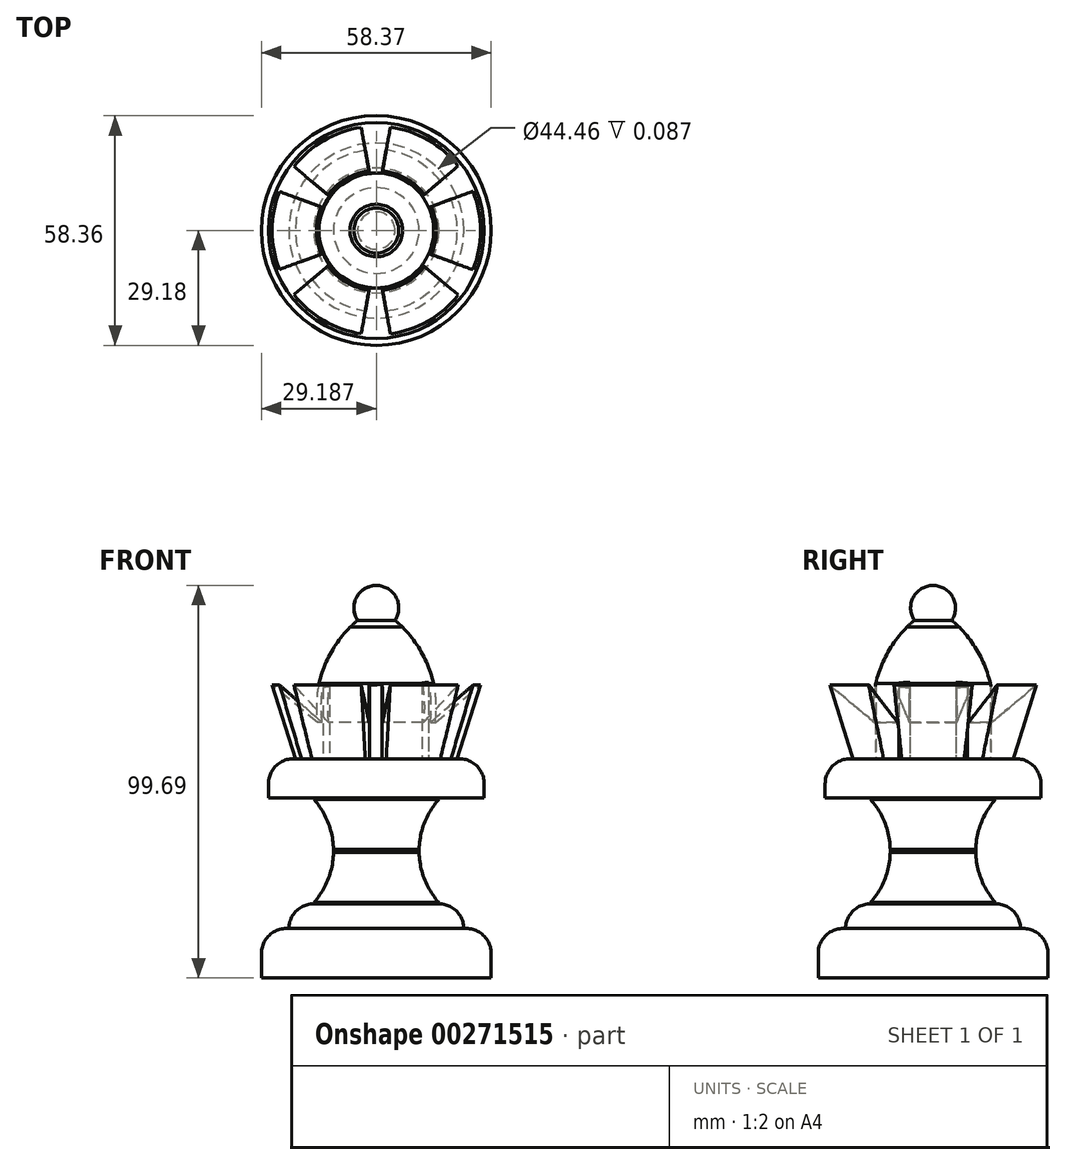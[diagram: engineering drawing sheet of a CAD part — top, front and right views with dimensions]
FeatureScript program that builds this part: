
annotation { "Feature Type Name" : "Feature", "Feature Type Description" : "" }
export const myFeature = defineFeature(function(context is Context, id is Id, definition is map)
    precondition{}
    {
        {
            var Q0;
            Q0=qCreatedBy(makeId("Front.planeOp"),FACE);
            var sketch = newSketch(context, id + "F0", { "sketchPlane" : qUnion([Q0])});
            skLineSegment(sketch, "E0.bottom", {"start": v(0.14, 0) * mm, "end": v(-29.05, 0) * mm});
            skLineSegment(sketch, "E0.top", {"start": v(-22.1, 12.55) * mm, "end": v(-22.7, 12.55) * mm});
            skLineSegment(sketch, "E0.right", {"start": v(-29.05, 0) * mm, "end": v(-29.05, 6.2) * mm});
            skLineSegment(sketch, "E1.bottom", {"start": v(-0.27, 12.55) * mm, "end": v(0, 12.55) * mm});
            skLineSegment(sketch, "E1.left", {"start": v(-22.1, 12.46) * mm, "end": v(-22.1, 12.55) * mm});
            skPoint(sketch, "E2.visualSharp", {"position": v(-29.05, 12.55) * mm});
            skArc(sketch, "E2.filletArc", {"start": v(-22.7, 12.55) * mm, "mid": v(-27.19, 10.69) * mm, "end": v(-29.05, 6.2) * mm});
            skPoint(sketch, "E3.visualSharp", {"position": v(-22.1, 18.81) * mm});
            skArc(sketch, "E3.filletArc", {"start": v(-15.74, 18.81) * mm, "mid": v(-20.23, 16.95) * mm, "end": v(-22.1, 12.46) * mm});
            skLineSegment(sketch, "E4.top", {"start": v(-36.14, 45.67) * mm, "end": v(-36.14, 45.67) * mm});
            skLineSegment(sketch, "E4.left", {"start": v(-15.74, 18.81) * mm, "end": v(-15.74, 19.14) * mm});
            skLineSegment(sketch, "E5.bottom", {"start": v(-27.27, 45.67) * mm, "end": v(-15.74, 45.67) * mm});
            skLineSegment(sketch, "E5.top", {"start": v(-20.92, 55.67) * mm, "end": v(-20.41, 55.67) * mm});
            skLineSegment(sketch, "E5.left", {"start": v(-27.27, 45.67) * mm, "end": v(-27.27, 49.32) * mm});
            skPoint(sketch, "E6.visualSharp", {"position": v(-14.84, 64.87) * mm});
            skPoint(sketch, "E7.visualSharp", {"position": v(-27.27, 55.67) * mm});
            skArc(sketch, "E7.filletArc", {"start": v(-20.92, 55.67) * mm, "mid": v(-25.41, 53.81) * mm, "end": v(-27.27, 49.32) * mm});
            skLineSegment(sketch, "E8.trimOffspring", {"start": v(-15.74, 45.33) * mm, "end": v(-15.74, 45.67) * mm});
            skPoint(sketch, "E5.right.end.orphan", {"position": v(0, 55.67) * mm});
            skPoint(sketch, "E1.right.end.orphan", {"position": v(0, 18.81) * mm});
            skPoint(sketch, "E9.center.orphan", {"position": v(-15.74, 32.24) * mm});
            skLineSegment(sketch, "E10", {"start": v(-15.74, 45.67) * mm, "end": v(-15.74, 45.33) * mm});
            skLineSegment(sketch, "E11.0", {"start": v(-10.74, 32.61) * mm, "end": v(-10.74, 31.86) * mm});
            skArc(sketch, "E12", {"start": v(-15.74, 19.14) * mm, "mid": v(-10.74, 32.24) * mm, "end": v(-15.74, 45.33) * mm});
            skLineSegment(sketch, "E13", {"start": v(-26.35, 74.38) * mm, "end": v(-14.84, 64.87) * mm});
            skPoint(sketch, "E14.top.end.orphan", {"position": v(0, 64.87) * mm});
            skArc(sketch, "E15", {"start": v(-4.61, 90.83) * mm, "mid": v(-5.6, 89.98) * mm, "end": v(-6.55, 89.1) * mm});
            skLineSegment(sketch, "E16", {"start": v(0.14, 93.98) * mm, "end": v(0.14, 0) * mm});
            skPoint(sketch, "E17.orphan", {"position": v(-0.27, 0) * mm});
            skArc(sketch, "E18.trimOffspring", {"start": v(-14.43, 74.8) * mm, "mid": v(-15.07, 69.85) * mm, "end": v(-14.84, 64.87) * mm});
            skArc(sketch, "E19", {"start": v(-6.55, 89.1) * mm, "mid": v(-11.46, 82.48) * mm, "end": v(-14.43, 74.8) * mm});
            skLineSegment(sketch, "E20", {"start": v(-20.41, 55.67) * mm, "end": v(-26.35, 74.38) * mm});
            skArc(sketch, "E21", {"start": v(0.14, 99.69) * mm, "mid": v(-5.56, 93.98) * mm, "end": v(0.14, 88.28) * mm});
            skLineSegment(sketch, "E22", {"start": v(0.14, 93.98) * mm, "end": v(0.14, 99.69) * mm});
            skSolve(sketch);
        }
        {
            var Q0;
            Q0 = qSketchRegion(id + "F0", true);
            var Q1;
            Q1 = qSketchRegion(id + "F2", true);
            var Q2;
            Q2=sQuery(id+"F0.wireOp",EDGE,"E16");
            revolve(context, id + "F1", {"entities" : qUnion([Q0, Q1]), "axis" : qUnion([Q2]), "revolveType" : RevolveType.FULL});
        }
        {
            var Q0;
            Q0=qCreatedBy(makeId("Front.planeOp"),FACE);
            var sketch = newSketch(context, id + "F2", { "sketchPlane" : qUnion([Q0])});
            skSolve(sketch);
        }
        {
            var Q0;
            Q0=makeQuery(id+"F1.opRevolve","SWEPT_FACE",FACE,{"disambiguationData":[OSD([sQuery(id+"F0.wireOp",EDGE,"E5.top")])]});
            var sketch = newSketch(context, id + "F3", { "sketchPlane" : qUnion([Q0])});
            skArc(sketch, "E23", {"start": v(1.63, 14.55) * mm, "mid": v(0, 14.64) * mm, "end": v(-1.63, 14.55) * mm});
            skLineSegment(sketch, "E24", {"start": v(1.63, 14.55) * mm, "end": v(4.94, 33.28) * mm});
            skLineSegment(sketch, "E25", {"start": v(-4.94, 33.28) * mm, "end": v(-1.63, 14.55) * mm});
            skPoint(sketch, "E26.start.orphan", {"position": v(0, 14.64) * mm});
            skArc(sketch, "E27", {"start": v(4.94, 33.28) * mm, "mid": v(0, 33.64) * mm, "end": v(-4.94, 33.28) * mm});
            skLineSegment(sketch, "E28.1.0", {"start": v(-11.78, 8.7) * mm, "end": v(-26.35, 20.91) * mm});
            skArc(sketch, "E28.1.1", {"start": v(-26.35, 20.91) * mm, "mid": v(-29.14, 16.82) * mm, "end": v(-31.29, 12.36) * mm});
            skLineSegment(sketch, "E28.1.2", {"start": v(-31.29, 12.36) * mm, "end": v(-13.42, 5.86) * mm});
            skArc(sketch, "E28.1.3", {"start": v(-11.78, 8.7) * mm, "mid": v(-12.68, 7.32) * mm, "end": v(-13.42, 5.86) * mm});
            skLineSegment(sketch, "E28.2.0", {"start": v(-13.42, -5.86) * mm, "end": v(-31.29, -12.36) * mm});
            skArc(sketch, "E28.2.1", {"start": v(-31.29, -12.36) * mm, "mid": v(-29.14, -16.82) * mm, "end": v(-26.35, -20.91) * mm});
            skLineSegment(sketch, "E28.2.2", {"start": v(-26.35, -20.91) * mm, "end": v(-11.78, -8.7) * mm});
            skArc(sketch, "E28.2.3", {"start": v(-13.42, -5.86) * mm, "mid": v(-12.68, -7.32) * mm, "end": v(-11.78, -8.7) * mm});
            skLineSegment(sketch, "E28.3.0", {"start": v(-1.63, -14.55) * mm, "end": v(-4.94, -33.28) * mm});
            skArc(sketch, "E28.3.1", {"start": v(-4.94, -33.28) * mm, "mid": v(0, -33.64) * mm, "end": v(4.94, -33.28) * mm});
            skLineSegment(sketch, "E28.3.2", {"start": v(4.94, -33.28) * mm, "end": v(1.63, -14.55) * mm});
            skArc(sketch, "E28.3.3", {"start": v(-1.63, -14.55) * mm, "mid": v(0, -14.64) * mm, "end": v(1.63, -14.55) * mm});
            skLineSegment(sketch, "E28.4.0", {"start": v(11.78, -8.7) * mm, "end": v(26.35, -20.91) * mm});
            skArc(sketch, "E28.4.1", {"start": v(26.35, -20.91) * mm, "mid": v(29.14, -16.82) * mm, "end": v(31.29, -12.36) * mm});
            skLineSegment(sketch, "E28.4.2", {"start": v(31.29, -12.36) * mm, "end": v(13.42, -5.86) * mm});
            skArc(sketch, "E28.4.3", {"start": v(11.78, -8.7) * mm, "mid": v(12.68, -7.32) * mm, "end": v(13.42, -5.86) * mm});
            skLineSegment(sketch, "E28.5.0", {"start": v(13.42, 5.86) * mm, "end": v(31.29, 12.36) * mm});
            skArc(sketch, "E28.5.1", {"start": v(31.29, 12.36) * mm, "mid": v(29.14, 16.82) * mm, "end": v(26.35, 20.91) * mm});
            skLineSegment(sketch, "E28.5.2", {"start": v(26.35, 20.91) * mm, "end": v(11.78, 8.7) * mm});
            skArc(sketch, "E28.5.3", {"start": v(13.42, 5.86) * mm, "mid": v(12.68, 7.32) * mm, "end": v(11.78, 8.7) * mm});
            skSolve(sketch);
        }
        {
            var Q0;
            Q0 = qSketchRegion(id + "F3", true);
            extrude(context, id + "F4", {"entities" : qUnion([Q0]), "operationType" : NewBodyOperationType.REMOVE, "depth" : 25 * mm});
        }
    });
